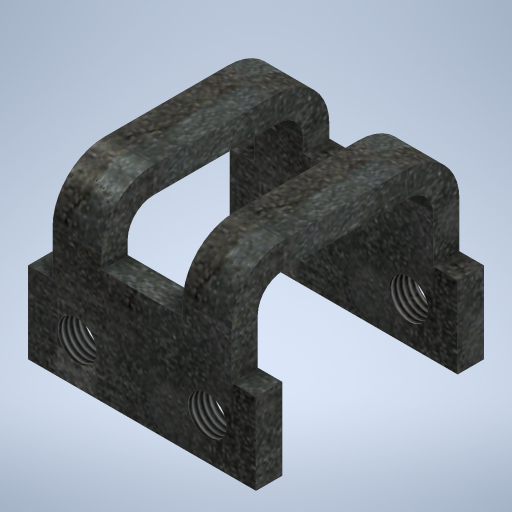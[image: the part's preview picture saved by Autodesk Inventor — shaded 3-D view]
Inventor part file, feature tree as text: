
AUTODESK INVENTOR PART (.ipt)
format: ipt  version: 2024 (Build 280153000, 153)  size: 587,264 bytes
history: native  units: mm
features: sheet_metal_op x7, thread x4, sketch x4, other x3, plane x1, mirror x1, extrude x1
ambient origin geometry x8: Origin, YZ Plane, XZ Plane, XY Plane, X Axis, Y Axis, Z Axis, Center Point
bodies: Solid1 (feature_tree)
feature tree (21):
  sheet_metal_op  "Face1"
  sheet_metal_op  "Flange1"
  plane  "Work Plane2"
  mirror  "Mirror1"
  sheet_metal_op  "Flange4"
  extrude  "Extrusion1"  Depth=8.0mm
  thread  "Thread9"  [1 undecoded]
  thread  "Thread10"  [1 undecoded]
  thread  "Thread11"  [1 undecoded]
  thread  "Thread12"  [1 undecoded]
  sketch  "Sketch1"  dims[d8=25.0mm d12=8.0mm d13=8.0mm d14=4.0mm d15=16.0mm d16=8.0mm]
  other  "Plate1"
  sketch  "Sketch2"  dims[d17=35.0mm d18=90.0deg d19=8.0mm]
  other  "Plate2"
  sheet_metal_op  "Bend1"
  sheet_metal_op  "Corner1"
  sketch  "Sketch6"  dims[d20=32.0mm]
  other  "Plate5"
  sheet_metal_op  "Bend4"
  sheet_metal_op  "Corner4"
  sketch  "Sketch7"  dims[d21=8.0mm d22=8.0mm d44=-35.0mm d45=8.0mm d46=4.0mm d47=16.0mm d48=8.0mm d49=35.0mm d50=90.0deg d51=8.0mm d52=32.0mm d53=8.0mm d54=8.0mm d55=12.0mm d56=12.0mm d57=40.0mm d61=80.0mm d62=0.0mm d116=55.0mm d128=30.0mm d129=7.5mm d130=25.0mm d131=70.0mm d132=90.0deg d133=25.0mm d134=7.5mm d135=27.5mm d136=0.0mm d137=15.0mm d138=12.5mm d139=20.0mm d140=350.0mm d141=0.0mm d142=350.0mm d143=0.0mm d144=350.0mm d145=0.0mm d146=350.0mm d147=0.0mm]
note: 4 required parameter values undecoded (feature->parameter linkage not recoverable at this tier; creation-order binding heuristic only, values carry confidence <= 0.55)
